FCSTD DOCUMENT  (FreeCAD 1.0R39319 (Git))
Label: sketch2
License: All rights reserved
LicenseURL: https://en.wikipedia.org/wiki/All_rights_reserved
objects: Sketcher::SketchObject×1, PartDesign::Body×1
note: 3 computed .brp shape members not serialized (recipe doc carries the construction recipe); baked Part::Feature solids carry a one-line shape summary decoded from their .brp

FEATURE [Sketcher::SketchObject] Sketch
  ArcFitTolerance = 1e-06
  AttachmentSupport = -> [XZ_Plane]
  FullyConstrained = true
  MakeInternals = false
  MapMode = 5
  Placement = pos=(0,0,0) rot=(1,0,0;1.5708rad)
  sketch-geometry (15):
    g0: Circle CenterX=0 CenterY=100.416 CenterZ=0 NormalX=0 NormalY=0 NormalZ=1 AngleXU=0 Radius=7.5
    g1: Circle CenterX=60 CenterY=30.4161 CenterZ=0 NormalX=0 NormalY=0 NormalZ=1 AngleXU=0 Radius=7.5
    g2: ArcOfCircle CenterX=0 CenterY=65.4161 CenterZ=0 NormalX=0 NormalY=0 NormalZ=1 AngleXU=0 Radius=50 StartAngle=5.8333 EndAngle=7.85398
    g3: ArcOfCircle CenterX=0 CenterY=100.416 CenterZ=0 NormalX=0 NormalY=0 NormalZ=1 AngleXU=0 Radius=15 StartAngle=1.5708 EndAngle=3.14159
    g4: LineSegment StartX=-15 StartY=100.416 StartZ=0 EndX=-15 EndY=70.4161 EndZ=0
    g5: LineSegment StartX=-5 StartY=60.4161 StartZ=0 EndX=5 EndY=60.4161 EndZ=0
    g6: ArcOfCircle CenterX=-5 CenterY=70.4161 CenterZ=0 NormalX=0 NormalY=0 NormalZ=1 AngleXU=0 Radius=10 StartAngle=3.14159 EndAngle=4.71239
    g7: GeomPoint [constr] X=-15 Y=60.4161 Z=0
    g8: ArcOfCircle CenterX=60 CenterY=30.4161 CenterZ=0 NormalX=0 NormalY=0 NormalZ=1 AngleXU=0 Radius=20 StartAngle=4.71239 EndAngle=8.70017
    g9: LineSegment StartX=60 StartY=10.4161 StartZ=0 EndX=45 EndY=10.4161 EndZ=0
    g10: LineSegment StartX=15 StartY=50.4161 StartZ=0 EndX=15 EndY=40.4161 EndZ=0
    g11: ArcOfCircle CenterX=45 CenterY=40.4161 CenterZ=0 NormalX=0 NormalY=0 NormalZ=1 AngleXU=0 Radius=30 StartAngle=3.14159 EndAngle=4.71239
    g12: GeomPoint [constr] X=15 Y=10.4161 Z=0
    g13: ArcOfCircle CenterX=5 CenterY=50.4161 CenterZ=0 NormalX=0 NormalY=0 NormalZ=1 AngleXU=0 Radius=10 StartAngle=2e-16 EndAngle=1.5708
    g14: GeomPoint [constr] X=15 Y=60.4161 Z=0
  constraints (38):
    c: PointOnObject(g0,g-2)
    c: DistanceX(g0,g1) = 60
    c: Diameter(g0) = 15
    c: Equal(g0,g1)
    c: PointOnObject(g2,g-2)
    c: Radius(g2) = 50
    c: DistanceY(g1,g0) = 70
    c: Tangent(g2,g3) = -1.5708
    c: Coincident(g3,g0)
    c: Radius(g3) = 15
    c: Horizontal(g0,g3)
    c: Coincident(g4,g3)
    c: Vertical(g4)
    c: DistanceY(g7,g4) = 40
    c: Distance(g14,g7) = 30
    c: Horizontal(g5)
    c: PointOnObject(g7,g4)
    c: PointOnObject(g7,g5)
    c: Tangent(g4,g6) = -1.5708
    c: Tangent(g5,g6) = -1.5708
    c: Radius(g6) = 10
    c: Coincident(g8,g1)
    c: Diameter(g8) = 40
    c: Distance(g9,g12) = 45
    c: Horizontal(g9)
    c: PointOnObject(g12,g10)
    c: PointOnObject(g12,g9)
    c: Tangent(g10,g11) = -1.5708
    c: Tangent(g9,g11) = 1.5708
    c: Radius(g11) = 30
    c: Coincident(g8,g2)
    c: Tangent(g8,g9) = 1.5708
    c: PointOnObject(g14,g5)
    c: PointOnObject(g14,g10)
    c: Tangent(g5,g13) = 1.5708
    c: Tangent(g10,g13) = 1.5708
    c: Radius(g13) = 10
    c: Block(g8)
FEATURE [PartDesign::Body] Body
  AllowCompound = false
  Group = -> [Sketch]
  Origin = -> Origin
